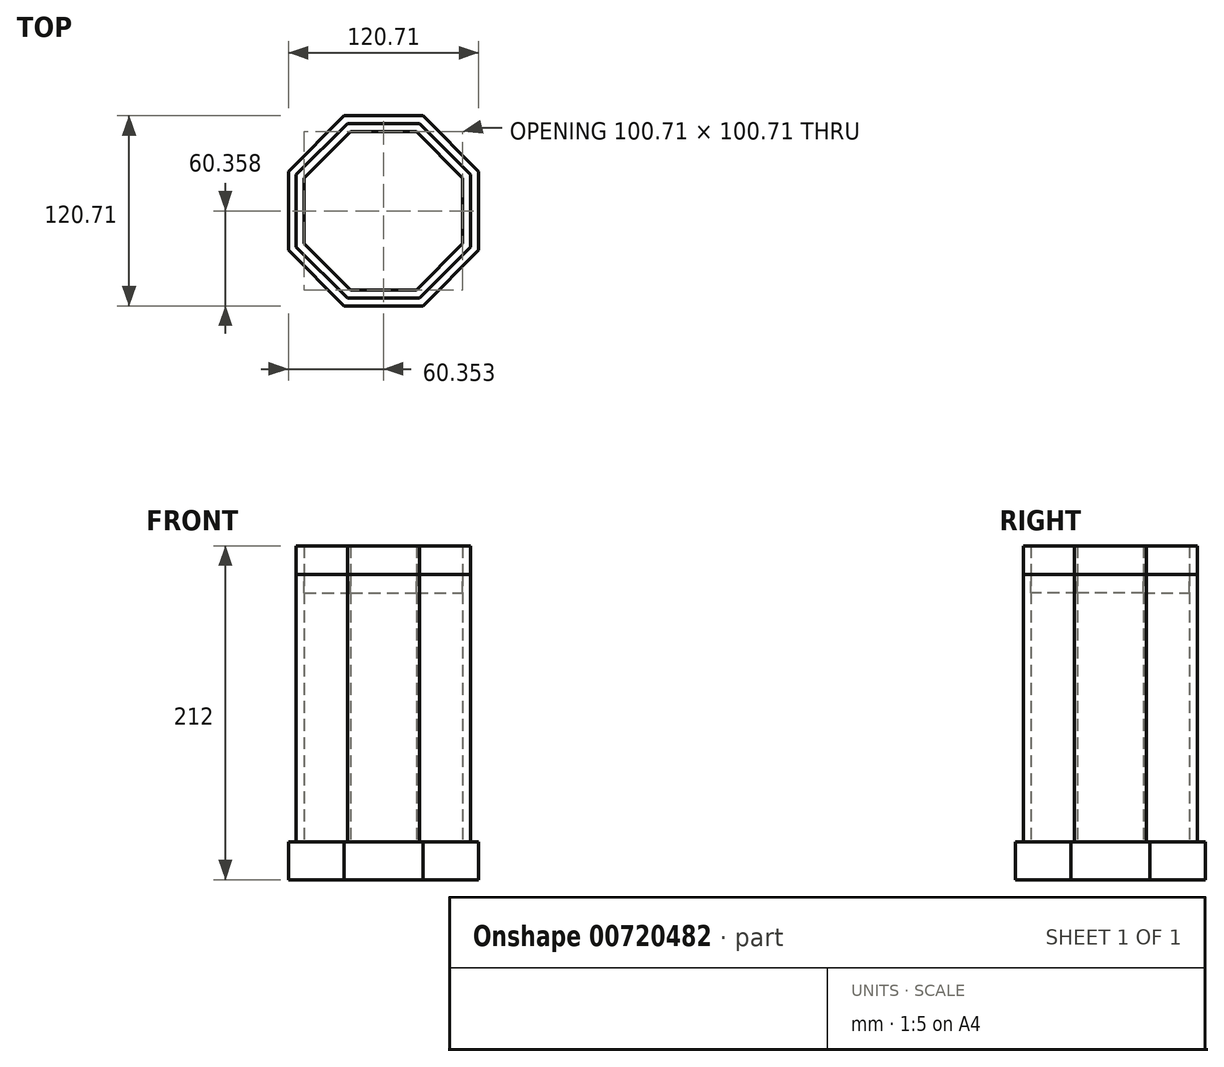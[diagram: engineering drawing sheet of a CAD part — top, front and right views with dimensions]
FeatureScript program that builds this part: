
annotation { "Feature Type Name" : "Feature", "Feature Type Description" : "" }
export const myFeature = defineFeature(function(context is Context, id is Id, definition is map)
    precondition{}
    {
        {
            var Q0;
            Q0=qCreatedBy(makeId("Top.planeOp"),FACE);
            var sketch = newSketch(context, id + "F0", { "sketchPlane" : qUnion([Q0])});
            skLineSegment(sketch, "E0", {"start": v(-22.36, -61.2) * mm, "end": v(27.64, -61.2) * mm});
            skLineSegment(sketch, "E1", {"start": v(27.64, -61.2) * mm, "end": v(63, -25.85) * mm});
            skLineSegment(sketch, "E2", {"start": v(63, -25.85) * mm, "end": v(63, 24.15) * mm});
            skLineSegment(sketch, "E3", {"start": v(63, 24.15) * mm, "end": v(27.64, 59.5) * mm});
            skLineSegment(sketch, "E4", {"start": v(27.64, 59.5) * mm, "end": v(-22.36, 59.5) * mm});
            skLineSegment(sketch, "E5", {"start": v(-22.36, 59.5) * mm, "end": v(-57.71, 24.15) * mm});
            skLineSegment(sketch, "E6", {"start": v(-57.71, 24.15) * mm, "end": v(-57.71, -25.85) * mm});
            skLineSegment(sketch, "E7", {"start": v(-57.71, -25.85) * mm, "end": v(-22.36, -61.2) * mm});
            skLineSegment(sketch, "E8", {"start": v(2.64, 59.5) * mm, "end": v(2.64, -61.2) * mm});
            skLineSegment(sketch, "E9", {"start": v(-57.71, -0.85) * mm, "end": v(63, -0.85) * mm});
            skLineSegment(sketch, "E10", {"start": v(-50.64, -0.85) * mm, "end": v(2.64, -0.85) * mm});
            skLineSegment(sketch, "E11", {"start": v(58, -0.85) * mm, "end": v(2.64, -0.85) * mm});
            skLineSegment(sketch, "E12", {"start": v(2.64, -0.85) * mm, "end": v(-50.64, -0.85) * mm});
            skLineSegment(sketch, "E13", {"start": v(2.64, -0.85) * mm, "end": v(63, -0.85) * mm});
            skLineSegment(sketch, "E14", {"start": v(2.64, -0.85) * mm, "end": v(-57.71, -0.85) * mm});
            skLineSegment(sketch, "E15", {"start": v(-57.71, -0.85) * mm, "end": v(2.64, -0.85) * mm});
            skLineSegment(sketch, "E16.0", {"start": v(25.57, 54.5) * mm, "end": v(-20.29, 54.5) * mm});
            skLineSegment(sketch, "E16.1", {"start": v(58, 22.08) * mm, "end": v(25.57, 54.5) * mm});
            skLineSegment(sketch, "E16.2", {"start": v(-20.29, 54.5) * mm, "end": v(-52.71, 22.08) * mm});
            skLineSegment(sketch, "E16.3", {"start": v(58, -23.78) * mm, "end": v(58, 22.08) * mm});
            skLineSegment(sketch, "E16.4", {"start": v(-52.71, 22.08) * mm, "end": v(-52.71, -23.78) * mm});
            skLineSegment(sketch, "E16.5", {"start": v(-52.71, -23.78) * mm, "end": v(-20.29, -56.2) * mm});
            skLineSegment(sketch, "E16.6", {"start": v(-20.29, -56.2) * mm, "end": v(25.57, -56.2) * mm});
            skLineSegment(sketch, "E16.7", {"start": v(25.57, -56.2) * mm, "end": v(58, -23.78) * mm});
            skLineSegment(sketch, "E17.0", {"start": v(-68.3, 102.52) * mm, "end": v(-100.73, 70.1) * mm});
            skLineSegment(sketch, "E18.0", {"start": v(23.5, 49.5) * mm, "end": v(-18.21, 49.5) * mm});
            skLineSegment(sketch, "E18.1", {"start": v(53, 20) * mm, "end": v(23.5, 49.5) * mm});
            skLineSegment(sketch, "E18.2", {"start": v(-18.21, 49.5) * mm, "end": v(-47.71, 20) * mm});
            skLineSegment(sketch, "E18.3", {"start": v(53, -21.7) * mm, "end": v(53, 20) * mm});
            skLineSegment(sketch, "E18.4", {"start": v(-47.71, 20) * mm, "end": v(-47.71, -21.7) * mm});
            skLineSegment(sketch, "E18.5", {"start": v(-47.71, -21.7) * mm, "end": v(-18.21, -51.2) * mm});
            skLineSegment(sketch, "E18.6", {"start": v(-18.21, -51.2) * mm, "end": v(23.5, -51.2) * mm});
            skLineSegment(sketch, "E18.7", {"start": v(23.5, -51.2) * mm, "end": v(53, -21.7) * mm});
            skLineSegment(sketch, "E19", {"start": v(-20.29, 54.5) * mm, "end": v(-18.21, 49.5) * mm});
            skLineSegment(sketch, "E20", {"start": v(23.5, 49.5) * mm, "end": v(25.57, 54.5) * mm});
            skLineSegment(sketch, "E21", {"start": v(53, 20) * mm, "end": v(58, 22.08) * mm});
            skSolve(sketch);
        }
        {
            var Q0;
            {var subQ0=sQuery(id+"F0.wireOp",EDGE,"E18.2");Q0=makeQuery(id+"F0.imprint","IMPRINT",FACE,{"disambiguationData":[TD([[makeQuery(id+"F0.imprint","IMPRINT",EDGE,{"derivedFrom":subQ0}),1.0]])]});}
            var Q1;
            {var subQ0=sQuery(id+"F0.wireOp",EDGE,"E18.5");Q1=makeQuery(id+"F0.imprint","IMPRINT",FACE,{"disambiguationData":[TD([[makeQuery(id+"F0.imprint","IMPRINT",EDGE,{"derivedFrom":subQ0}),1.0]])]});}
            var Q2;
            {var subQ0=sQuery(id+"F0.wireOp",EDGE,"E18.7");Q2=makeQuery(id+"F0.imprint","IMPRINT",FACE,{"disambiguationData":[TD([[makeQuery(id+"F0.imprint","IMPRINT",EDGE,{"derivedFrom":subQ0}),1.0]])]});}
            var Q3;
            {var subQ0=sQuery(id+"F0.wireOp",EDGE,"E18.1");Q3=makeQuery(id+"F0.imprint","IMPRINT",FACE,{"disambiguationData":[TD([[makeQuery(id+"F0.imprint","IMPRINT",EDGE,{"derivedFrom":subQ0}),1.0]])]});}
            var Q4;
            Q4=makeQuery(id+"F0.imprint","IMPRINT",FACE,{"disambiguationData":[TD([[makeQuery(id+"F0.imprint","IMPRINT",EDGE,{"derivedFrom":sQuery(id+"F0.wireOp",EDGE,"E16.1")}),1.0]])]});
            var Q5;
            {var subQ5=sQuery(id+"F0.wireOp",EDGE,"E21");Q5=makeQuery(id+"F0.imprint","IMPRINT",FACE,{"disambiguationData":[TD([[makeQuery(id+"F0.imprint","IMPRINT",EDGE,{"derivedFrom":subQ5}),-1.0]])]});}
            var Q6;
            {var subQ0=sQuery(id+"F0.wireOp",EDGE,"E16.7");Q6=makeQuery(id+"F0.imprint","IMPRINT",FACE,{"disambiguationData":[TD([[makeQuery(id+"F0.imprint","IMPRINT",EDGE,{"derivedFrom":subQ0}),1.0]])]});}
            var Q7;
            {var subQ5=sQuery(id+"F0.wireOp",EDGE,"E16.5");Q7=makeQuery(id+"F0.imprint","IMPRINT",FACE,{"disambiguationData":[TD([[makeQuery(id+"F0.imprint","IMPRINT",EDGE,{"derivedFrom":subQ5}),1.0]])]});}
            var Q8;
            {var subQ1=sQuery(id+"F0.wireOp",EDGE,"E16.2");Q8=makeQuery(id+"F0.imprint","IMPRINT",FACE,{"disambiguationData":[TD([[makeQuery(id+"F0.imprint","IMPRINT",EDGE,{"derivedFrom":subQ1}),1.0]])]});}
            var Q9;
            {var subQ5=sQuery(id+"F0.wireOp",EDGE,"E19");Q9=makeQuery(id+"F0.imprint","IMPRINT",FACE,{"disambiguationData":[TD([[makeQuery(id+"F0.imprint","IMPRINT",EDGE,{"derivedFrom":subQ5}),1.0]])]});}
            var Q10;
            {var subQ5=sQuery(id+"F0.wireOp",EDGE,"E20");Q10=makeQuery(id+"F0.imprint","IMPRINT",FACE,{"disambiguationData":[TD([[makeQuery(id+"F0.imprint","IMPRINT",EDGE,{"derivedFrom":subQ5}),1.0]])]});}
            var Q11;
            {var subQ5=sQuery(id+"F0.wireOp",EDGE,"E3");Q11=makeQuery(id+"F0.imprint","IMPRINT",FACE,{"disambiguationData":[TD([[makeQuery(id+"F0.imprint","IMPRINT",EDGE,{"derivedFrom":subQ5}),1.0]])]});}
            var Q12;
            {var subQ1=sQuery(id+"F0.wireOp",EDGE,"E5");Q12=makeQuery(id+"F0.imprint","IMPRINT",FACE,{"disambiguationData":[TD([[makeQuery(id+"F0.imprint","IMPRINT",EDGE,{"derivedFrom":subQ1}),1.0]])]});}
            var Q13;
            {var subQ5=sQuery(id+"F0.wireOp",EDGE,"E7");Q13=makeQuery(id+"F0.imprint","IMPRINT",FACE,{"disambiguationData":[TD([[makeQuery(id+"F0.imprint","IMPRINT",EDGE,{"derivedFrom":subQ5}),1.0]])]});}
            var Q14;
            {var subQ1=sQuery(id+"F0.wireOp",EDGE,"E1");Q14=makeQuery(id+"F0.imprint","IMPRINT",FACE,{"disambiguationData":[TD([[makeQuery(id+"F0.imprint","IMPRINT",EDGE,{"derivedFrom":subQ1}),1.0]])]});}
            extrude(context, id + "F1", {"entities" : qUnion([Q0, Q1, Q2, Q3, Q4, Q5, Q6, Q7, Q8, Q9, Q10, Q11, Q12, Q13, Q14]), "oppositeDirection" : true, "depth" : 24 * mm, "offsetDistance" : 25 * mm});
        }
        {
            var Q0;
            {var subQ1=sQuery(id+"F0.wireOp",EDGE,"E16.2");Q0=makeQuery(id+"F0.imprint","IMPRINT",FACE,{"disambiguationData":[TD([[makeQuery(id+"F0.imprint","IMPRINT",EDGE,{"derivedFrom":subQ1}),1.0]])]});}
            var Q1;
            {var subQ5=sQuery(id+"F0.wireOp",EDGE,"E19");Q1=makeQuery(id+"F0.imprint","IMPRINT",FACE,{"disambiguationData":[TD([[makeQuery(id+"F0.imprint","IMPRINT",EDGE,{"derivedFrom":subQ5}),1.0]])]});}
            var Q2;
            {var subQ5=sQuery(id+"F0.wireOp",EDGE,"E20");Q2=makeQuery(id+"F0.imprint","IMPRINT",FACE,{"disambiguationData":[TD([[makeQuery(id+"F0.imprint","IMPRINT",EDGE,{"derivedFrom":subQ5}),1.0]])]});}
            var Q3;
            Q3=makeQuery(id+"F0.imprint","IMPRINT",FACE,{"disambiguationData":[TD([[makeQuery(id+"F0.imprint","IMPRINT",EDGE,{"derivedFrom":sQuery(id+"F0.wireOp",EDGE,"E16.1")}),1.0]])]});
            var Q4;
            {var subQ5=sQuery(id+"F0.wireOp",EDGE,"E21");Q4=makeQuery(id+"F0.imprint","IMPRINT",FACE,{"disambiguationData":[TD([[makeQuery(id+"F0.imprint","IMPRINT",EDGE,{"derivedFrom":subQ5}),-1.0]])]});}
            var Q5;
            {var subQ0=sQuery(id+"F0.wireOp",EDGE,"E16.7");Q5=makeQuery(id+"F0.imprint","IMPRINT",FACE,{"disambiguationData":[TD([[makeQuery(id+"F0.imprint","IMPRINT",EDGE,{"derivedFrom":subQ0}),1.0]])]});}
            var Q6;
            {var subQ5=sQuery(id+"F0.wireOp",EDGE,"E16.5");Q6=makeQuery(id+"F0.imprint","IMPRINT",FACE,{"disambiguationData":[TD([[makeQuery(id+"F0.imprint","IMPRINT",EDGE,{"derivedFrom":subQ5}),1.0]])]});}
            extrude(context, id + "F2", {"entities" : qUnion([Q0, Q1, Q2, Q3, Q4, Q5, Q6]), "operationType" : NewBodyOperationType.ADD, "depth" : 170 * mm, "offsetDistance" : 25 * mm});
        }
        {
            var Q0;
            Q0=makeQuery(id+"F2.opExtrude","CAP_FACE",FACE,{"disambiguationData":[OSD([sQuery(id+"F0.wireOp",EDGE,"E16.0"),sQuery(id+"F0.wireOp",EDGE,"E16.1"),sQuery(id+"F0.wireOp",EDGE,"E16.2"),sQuery(id+"F0.wireOp",EDGE,"E16.3"),sQuery(id+"F0.wireOp",EDGE,"E16.4"),sQuery(id+"F0.wireOp",EDGE,"E16.5"),sQuery(id+"F0.wireOp",EDGE,"E16.6"),sQuery(id+"F0.wireOp",EDGE,"E16.7"),sQuery(id+"F0.wireOp",EDGE,"E18.0"),sQuery(id+"F0.wireOp",EDGE,"E18.1"),sQuery(id+"F0.wireOp",EDGE,"E18.2"),sQuery(id+"F0.wireOp",EDGE,"E18.3"),sQuery(id+"F0.wireOp",EDGE,"E18.4"),sQuery(id+"F0.wireOp",EDGE,"E18.5"),sQuery(id+"F0.wireOp",EDGE,"E18.6"),sQuery(id+"F0.wireOp",EDGE,"E18.7")])],"isStart":false});
            var sketch = newSketch(context, id + "F3", { "sketchPlane" : qUnion([Q0])});
            skLineSegment(sketch, "E22", {"start": v(-47.71, 20) * mm, "end": v(-18.21, 49.5) * mm});
            skLineSegment(sketch, "E23", {"start": v(-18.21, 49.5) * mm, "end": v(23.5, 49.5) * mm});
            skLineSegment(sketch, "E24", {"start": v(23.5, 49.5) * mm, "end": v(53, 20) * mm});
            skLineSegment(sketch, "E25", {"start": v(53, 20) * mm, "end": v(53, -21.7) * mm});
            skLineSegment(sketch, "E26", {"start": v(53, -21.7) * mm, "end": v(23.5, -51.2) * mm});
            skLineSegment(sketch, "E27", {"start": v(23.5, -51.2) * mm, "end": v(-18.21, -51.2) * mm});
            skLineSegment(sketch, "E28", {"start": v(-18.21, -51.2) * mm, "end": v(-47.71, -21.7) * mm});
            skLineSegment(sketch, "E29", {"start": v(-47.71, -21.7) * mm, "end": v(-47.71, 20) * mm});
            skLineSegment(sketch, "E30", {"start": v(-52.71, 22.08) * mm, "end": v(-20.29, 54.5) * mm});
            skLineSegment(sketch, "E31", {"start": v(-20.29, 54.5) * mm, "end": v(25.57, 54.5) * mm});
            skLineSegment(sketch, "E32", {"start": v(25.57, 54.5) * mm, "end": v(58, 22.08) * mm});
            skLineSegment(sketch, "E33", {"start": v(58, 22.08) * mm, "end": v(58, -23.78) * mm});
            skLineSegment(sketch, "E34", {"start": v(58, -23.78) * mm, "end": v(25.57, -56.2) * mm});
            skLineSegment(sketch, "E35", {"start": v(25.57, -56.2) * mm, "end": v(-20.29, -56.2) * mm});
            skLineSegment(sketch, "E36", {"start": v(-20.29, -56.2) * mm, "end": v(-52.71, -23.78) * mm});
            skLineSegment(sketch, "E37", {"start": v(-52.71, -23.78) * mm, "end": v(-52.71, 22.08) * mm});
            skLineSegment(sketch, "E38.0", {"start": v(-57.71, 24.15) * mm, "end": v(-22.36, 59.5) * mm});
            skLineSegment(sketch, "E38.1", {"start": v(-57.71, -25.85) * mm, "end": v(-57.71, 24.15) * mm});
            skLineSegment(sketch, "E38.2", {"start": v(-22.36, 59.5) * mm, "end": v(27.64, 59.5) * mm});
            skLineSegment(sketch, "E38.3", {"start": v(-22.36, -61.2) * mm, "end": v(-57.71, -25.85) * mm});
            skLineSegment(sketch, "E38.4", {"start": v(27.64, 59.5) * mm, "end": v(63, 24.15) * mm});
            skLineSegment(sketch, "E38.5", {"start": v(63, 24.15) * mm, "end": v(63, -25.85) * mm});
            skLineSegment(sketch, "E38.6", {"start": v(63, -25.85) * mm, "end": v(27.64, -61.2) * mm});
            skLineSegment(sketch, "E38.7", {"start": v(27.64, -61.2) * mm, "end": v(-22.36, -61.2) * mm});
            skSolve(sketch);
        }
        {
            var Q0;
            Q0=makeQuery(id+"F3.imprint","IMPRINT",FACE,{"disambiguationData":[TD([[makeQuery(id+"F3.imprint","IMPRINT",EDGE,{"derivedFrom":sQuery(id+"F3.wireOp",EDGE,"E22")}),1.0]])]});
            extrude(context, id + "F4", {"entities" : qUnion([Q0]), "oppositeDirection" : true, "depth" : 12 * mm, "offsetDistance" : 25 * mm});
        }
        {
            var Q0;
            Q0=makeQuery(id+"F2.opExtrude","CAP_FACE",FACE,{"disambiguationData":[OSD([sQuery(id+"F0.wireOp",EDGE,"E16.0"),sQuery(id+"F0.wireOp",EDGE,"E16.1"),sQuery(id+"F0.wireOp",EDGE,"E16.2"),sQuery(id+"F0.wireOp",EDGE,"E16.3"),sQuery(id+"F0.wireOp",EDGE,"E16.4"),sQuery(id+"F0.wireOp",EDGE,"E16.5"),sQuery(id+"F0.wireOp",EDGE,"E16.6"),sQuery(id+"F0.wireOp",EDGE,"E16.7"),sQuery(id+"F0.wireOp",EDGE,"E18.0"),sQuery(id+"F0.wireOp",EDGE,"E18.1"),sQuery(id+"F0.wireOp",EDGE,"E18.2"),sQuery(id+"F0.wireOp",EDGE,"E18.3"),sQuery(id+"F0.wireOp",EDGE,"E18.4"),sQuery(id+"F0.wireOp",EDGE,"E18.5"),sQuery(id+"F0.wireOp",EDGE,"E18.6"),sQuery(id+"F0.wireOp",EDGE,"E18.7")])],"isStart":false});
            var Q1;
            Q1=makeQuery(id+"F4.opExtrude","CAP_FACE",FACE,{"disambiguationData":[OSD([sQuery(id+"F3.wireOp",EDGE,"E22"),sQuery(id+"F3.wireOp",EDGE,"E23"),sQuery(id+"F3.wireOp",EDGE,"E24"),sQuery(id+"F3.wireOp",EDGE,"E25"),sQuery(id+"F3.wireOp",EDGE,"E26"),sQuery(id+"F3.wireOp",EDGE,"E27"),sQuery(id+"F3.wireOp",EDGE,"E28"),sQuery(id+"F3.wireOp",EDGE,"E29")])],"isStart":true});
            extrude(context, id + "F5", {"entities" : qUnion([Q0, Q1]), "depth" : 18 * mm, "offsetDistance" : 25 * mm});
        }
    });
